# Revit family: Lagur STD
name_source: partatom
category: Plumbing Fixtures
units: mm (PartAtom-declared; Revit-internal decimal feet)

## family parameters
Always vertical = No
Cut with Voids When Loaded = No
OmniClass Number = 23.65.50.11.11.14
OmniClass Title = Water Softeners
Part Type = Normal
Room Calculation Point = No
Round Connector Dimension = Use Diameter
Shared = No
Work Plane-Based = No

## types (2) — shared parameters
HW Connection = No
IP Rating = IP54
Manufacturer = Lagur A/S
URL = https://lagur.dk
Uniclass2015Code = Ss_55_70
Uniclass2015Description = Water distribution and supply system
Vent Connection = No
Version = 1.0
Waste Connection = No
Watt = 25 W
X = 352 mm  [stored 1.15486 ft]
Y = 76 mm  [stored 0.249344 ft]
x = 37 mm  [stored 0.121391 ft]
zero-valued in all types: Default Elevation

## per-type parameters (varying)
| type | Model | Thread | Thread dimension in mm | Weight |
| DN20 | Lagur Pro DN20 | 3/4" RG. | 19 mm | 4.07 kg |
| DN25 | Lagur Pro DN25 | 1" RG. | 25 mm  [stored 0.082021 ft] | 4.85 kg |

note: [stored X ft] marks values corroborated as IEEE doubles in the binary element streams (Revit-internal decimal feet)

## geometry (parser evidence)
native form markers: Sweep x5
no freeform markers — native parametric forms only
